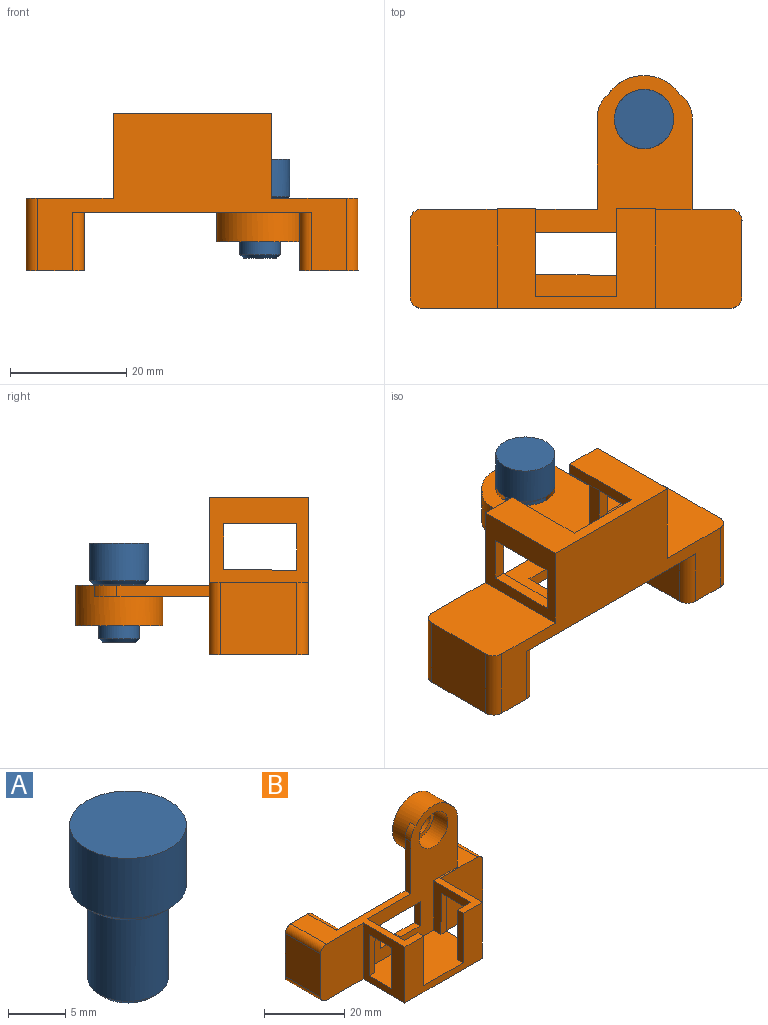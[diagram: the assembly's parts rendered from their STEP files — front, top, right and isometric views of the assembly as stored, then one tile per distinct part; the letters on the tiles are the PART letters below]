
ASSEMBLY  parts=2 mates=1
PART A: 7 faces, bbox 10.2x10.2x17 mm
  f0: plane 10.2x10.2mm, normal (0,0,1), area 81.7mm2, adj f4
  f1: plane 5.8x5.8mm, normal (0,0,-1), area 26.4mm2, adj f5
  f2: cylinder r=3.5mm len=9.4mm, axis (0,0,-1), area 206.7mm2, adj f3,f5
  f3: plane 9x9mm, normal (0,0,-1), area 25.1mm2, adj f2,f6
  f4: cylinder r=5.1mm len=10.2mm, axis (0,0,-1), area 205.1mm2, adj f0,f6
  f5: cone r=2.9mm half-angle=45deg, axis (0,0,1), area 17.1mm2, adj f1,f2
  f6: cone r=4.5mm half-angle=45deg, axis (0,0,1), area 25.6mm2, adj f3,f4
PART B: 51 faces, bbox 57.2x27.2x40.1 mm
  f0: plane 27.2x19.6mm, normal (0,0,1), area 119.4mm2, adj f1,f2,f4,f7,f10,f11,f20,f23
  f1: plane 17.1x14.7mm, normal (1,0,0), area 151.2mm2, adj f0,f4,f8,f12,f13,f14,f15,f23
  f2: plane 15.1x4.72mm, normal (0,1,0), area 71.3mm2, adj f0,f10,f12,f20
  f3: plane 15.1x4.6mm, normal (0,1,0), area 69.5mm2, adj f5,f9,f12,f19
  f4: plane 27.32x17.1mm, normal (0,-1,0), area 255.8mm2, adj f0,f1,f5,f6,f8,f12,f19,f20
  f5: plane 30.27x27.2mm, normal (0,0,1), area 166.6mm2, adj f3,f4,f6,f7,f9,f11,f19,f21
  f6: plane 17.1x14.7mm, normal (-1,0,0), area 151.2mm2, adj f4,f5,f8,f12,f16,f17,f18,f21
  f7: plane 41.2x36.9mm, normal (0,1,0), area 708.1mm2, adj f0,f5,f8,f25,f26,f27,f28,f29
  f8: plane 53.2x27.2mm, normal (0,0,-1), area 654.6mm2, adj f1,f4,f6,f7,f21,f23,f31,f33
  f9: plane 15.1x13.2mm, normal (1,0,0), area 99.1mm2, adj f3,f5,f11,f12,f16,f17,f18
  f10: plane 15.1x13.2mm, normal (-1,0,0), area 99.1mm2, adj f0,f2,f11,f12,f13,f14,f15
  f11: plane 38.1x31.64mm, normal (0,-1,0), area 515.7mm2, adj f0,f5,f9,f10,f12,f25,f26,f27
  f12: plane 27.32x15.2mm, normal (0,0,1), area 367.8mm2, adj f1,f2,f3,f4,f6,f9,f10,f11
  f13: plane 12.6x2mm, normal (0,-1,-0.01), area 25.2mm2, adj f1,f10,f12,f15
  f14: plane 12.6x2mm, normal (0,1,0), area 25.2mm2, adj f1,f10,f12,f15
  f15: plane 7.9x2mm, normal (0,0,-1), area 15.8mm2, adj f1,f10,f13,f14
  f16: plane 7.9x2mm, normal (0,0,-1), area 15.8mm2, adj f6,f9,f17,f18
  f17: plane 12.6x2mm, normal (0,1,0), area 25.2mm2, adj f6,f9,f12,f16
  f18: plane 12.6x2mm, normal (0,-1,-0.01), area 25.2mm2, adj f6,f9,f12,f16
  f19: plane 15.1x2mm, normal (1,0,0), area 30.2mm2, adj f3,f4,f5,f12
  f20: plane 15.1x2mm, normal (-1,0,0), area 30.2mm2, adj f0,f2,f4,f12
  f21: plane 17.1x15mm, normal (0,-1,0), area 254.8mm2, adj f5,f6,f8,f22,f40,f41
  f22: plane 13.1x12.5mm, normal (-1,0,0), area 163.8mm2, adj f21,f33,f40,f41
  f23: plane 17.1x14.88mm, normal (0,-1,0), area 252.7mm2, adj f0,f1,f8,f24,f38,f39
  f24: plane 13.1x12.5mm, normal (1,0,0), area 163.8mm2, adj f23,f31,f38,f39
  f25: plane 7x2mm, normal (0.02,0,1), area 14mm2, adj f7,f11,f26,f29
  f26: plane 7x2mm, normal (0,0,1), area 14mm2, adj f7,f11,f25,f27
  f27: plane 7.22x2mm, normal (1,0,0), area 14.4mm2, adj f7,f11,f26,f28
  f28: plane 14x2mm, normal (0,0,-1), area 28mm2, adj f7,f11,f27,f29
  f29: plane 7.36x2mm, normal (-1,0,0), area 14.7mm2, adj f7,f11,f25,f28
  f30: plane 13.1x10mm, normal (-1,0,0), area 131mm2, adj f7,f31,f36,f37
  f31: plane 17.1x10mm, normal (0,1,0), area 167.6mm2, adj f0,f8,f24,f30,f36,f37,f38,f39
  f32: plane 13.1x10mm, normal (1,0,0), area 131mm2, adj f7,f33,f34,f35
  f33: plane 17.1x10mm, normal (0,1,0), area 167.6mm2, adj f5,f8,f22,f32,f34,f35,f40,f41
  f34: cylinder r=2mm len=10mm, axis (0,1,0), area 31.4mm2, adj f5,f7,f32,f33
  f35: cylinder r=2mm len=10mm, axis (0,-1,0), area 31.4mm2, adj f7,f8,f32,f33
  f36: cylinder r=2mm len=10mm, axis (0,1,0), area 31.4mm2, adj f0,f7,f30,f31
  f37: cylinder r=2mm len=10mm, axis (0,-1,0), area 31.4mm2, adj f7,f8,f30,f31
  f38: cylinder r=2mm len=12.5mm, axis (0,-1,0), area 39.3mm2, adj f8,f23,f24,f31
  f39: cylinder r=2mm len=12.5mm, axis (0,1,0), area 39.3mm2, adj f0,f23,f24,f31
  f40: cylinder r=2mm len=12.5mm, axis (0,1,0), area 39.3mm2, adj f5,f21,f22,f33
  f41: cylinder r=2mm len=12.5mm, axis (0,-1,0), area 39.3mm2, adj f8,f21,f22,f33
  f42: plane 15.87x2mm, normal (-1,0,0), area 31.7mm2, adj f5,f7,f11,f47
  f43: plane 15.67x2mm, normal (1,0,0), area 31.3mm2, adj f0,f7,f11,f46
  f44: cylinder r=7.5mm len=15mm, axis (0,-1,0), area 264.4mm2, adj f7,f11,f45,f46,f47
  f45: plane 15x15mm, normal (0,1,0), area 126.4mm2, adj f44,f50
  f46: cylinder r=5mm len=4.13mm, axis (0,-1,0), area 9.7mm2, adj f7,f11,f43,f44
  f47: cylinder r=5mm len=3.93mm, axis (0,-1,0), area 9mm2, adj f7,f11,f42,f44
  f48: cylinder r=5.1mm len=10.2mm, axis (0,-1,0), area 160.2mm2, adj f11,f49
  f49: plane 10.2x10.2mm, normal (0,-1,0), area 31.4mm2, adj f48,f50
  f50: cylinder r=4mm len=8mm, axis (0,1,0), area 50.3mm2, adj f45,f49
PLACE A t=(-33.4,-0.61,29.38)mm
PLACE B rot(axis=(-1,0,0),90deg) t=(-45.12,-31.21,28.77)mm
MATE slider A.f2 <-> B.f44  axis (0,0,1) through (-33.4,-0.61,22.98)mm
